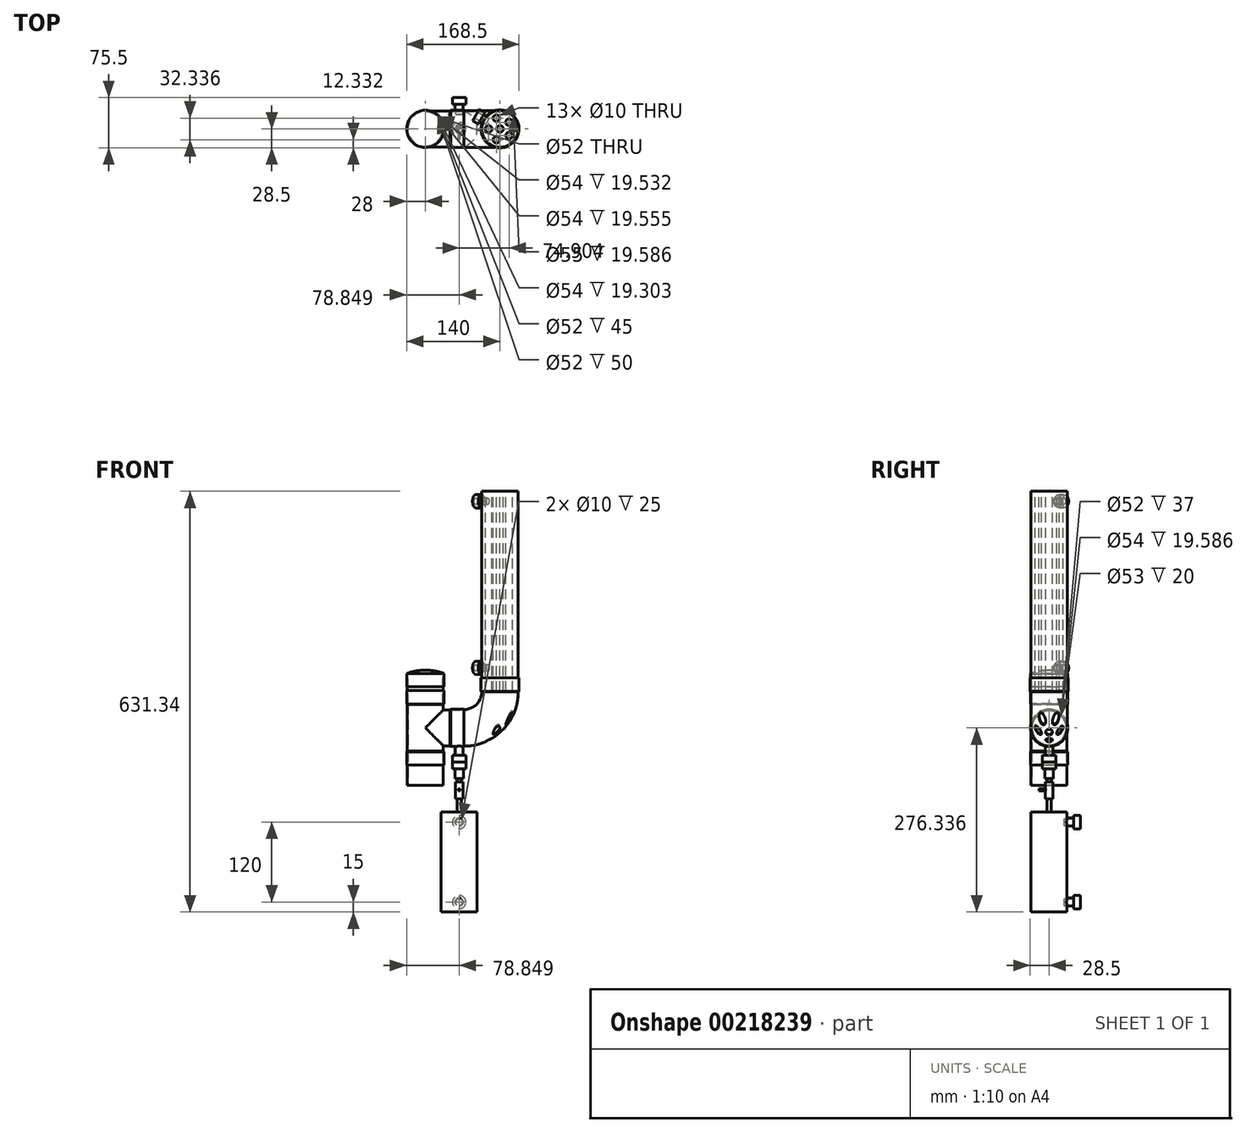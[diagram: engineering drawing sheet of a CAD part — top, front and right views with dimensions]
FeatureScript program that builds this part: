
annotation { "Feature Type Name" : "Feature", "Feature Type Description" : "" }
export const myFeature = defineFeature(function(context is Context, id is Id, definition is map)
    precondition{}
    {
        {
            var Q0;
            Q0=qCreatedBy(makeId("Top.planeOp"),FACE);
            var sketch = newSketch(context, id + "F0", { "sketchPlane" : qUnion([Q0])});
            skCircle(sketch, "E0", {"center": v(0, 0) * mm, "radius": 27 * mm});
            skCircle(sketch, "E1.0", {"center": v(0, 0) * mm, "radius": 26 * mm});
            skSolve(sketch);
        }
        {
            var Q0;
            Q0 = qSketchRegion(id + "F0", true);
            extrude(context, id + "F1", {"entities" : qUnion([Q0]), "depth" : 50 * mm, "symmetric" : true});
        }
        {
            var Q0;
            Q0=qCreatedBy(makeId("Front.planeOp"),FACE);
            var sketch = newSketch(context, id + "F2", { "sketchPlane" : qUnion([Q0])});
            skLineSegment(sketch, "E2", {"start": v(-27, 96.3) * mm, "end": v(-27, 26.3) * mm});
            skLineSegment(sketch, "E3", {"start": v(-27, 26.3) * mm, "end": v(-28, 25.47) * mm});
            skLineSegment(sketch, "E4", {"start": v(-28, 25.47) * mm, "end": v(-28, 5.47) * mm});
            skLineSegment(sketch, "E5", {"start": v(-28, 5.47) * mm, "end": v(-27, 5.47) * mm});
            skLineSegment(sketch, "E6", {"start": v(-27, 5.47) * mm, "end": v(-27, 25) * mm});
            skLineSegment(sketch, "E7", {"start": v(-27, 25) * mm, "end": v(-26, 25.83) * mm});
            skLineSegment(sketch, "E8", {"start": v(-26, 25.83) * mm, "end": v(-26, 96.75) * mm});
            skLineSegment(sketch, "E9.0", {"start": v(-27, 25) * mm, "end": v(27, 25) * mm, "construction": true});
            skLineSegment(sketch, "E10", {"start": v(-28, 25.47) * mm, "end": v(-28, 106.44) * mm, "construction": true});
            skLineSegment(sketch, "E11", {"start": v(-27, 96.3) * mm, "end": v(-28, 97.2) * mm});
            skLineSegment(sketch, "E12", {"start": v(-28, 97.2) * mm, "end": v(-28, 117.2) * mm});
            skLineSegment(sketch, "E13", {"start": v(-28, 117.2) * mm, "end": v(-27, 117.2) * mm});
            skLineSegment(sketch, "E14", {"start": v(-27, 117.2) * mm, "end": v(-27, 97.65) * mm});
            skLineSegment(sketch, "E15", {"start": v(-27, 97.65) * mm, "end": v(-26, 96.75) * mm});
            skSolve(sketch);
        }
        {
            var Q0;
            Q0 = qSketchRegion(id + "F2", true);
            var Q1;
            Q1=makeQuery(id+"F1.opExtrude","CAP_EDGE",EDGE,{"disambiguationData":[OSD([sQuery(id+"F0.wireOp",EDGE,"E0")])],"isStart":false});
            revolve(context, id + "F3", {"entities" : qUnion([Q0]), "axis" : qUnion([Q1]), "revolveType" : RevolveType.FULL});
        }
        {
            var Q0;
            Q0=qCreatedBy(makeId("Right.planeOp"),FACE);
            cPlane(context, id + "F4", {"entities" : qUnion([Q0]), "cplaneType" : CPlaneType.OFFSET, "offset" : (54 / 2 + 10) * mm, "width" : 150 * mm, "height" : 150 * mm});
        }
        {
            var Q0;
            Q0=qCreatedBy(id+"F4.planeOp",FACE);
            var sketch = newSketch(context, id + "F5", { "sketchPlane" : qUnion([Q0])});
            skCircle(sketch, "E16", {"center": v(0, 61.34) * mm, "radius": 27 * mm});
            skLineSegment(sketch, "E17.0", {"start": v(28, 117.2) * mm, "end": v(-28, 117.2) * mm, "construction": true});
            skLineSegment(sketch, "E18.0", {"start": v(28, 5.47) * mm, "end": v(-28, 5.47) * mm, "construction": true});
            skLineSegment(sketch, "E19", {"start": v(-40.75, 61.34) * mm, "end": v(41.53, 61.34) * mm, "construction": true});
            skSolve(sketch);
        }
        {
            var Q0;
            Q0 = qSketchRegion(id + "F5", true);
            var Q1;
            Q1=makeQuery(id+"F3.opRevolve","SWEPT_FACE",FACE,{"disambiguationData":[OSD([sQuery(id+"F2.wireOp",EDGE,"E2")])]});
            extrude(context, id + "F6", {"entities" : qUnion([Q0]), "operationType" : NewBodyOperationType.ADD, "endBound" : BoundingType.UP_TO_SURFACE, "oppositeDirection" : true, "endBoundEntityFace" : qUnion([Q1]), "depth" : 25 * mm});
        }
        {
            var Q0;
            Q0=makeQuery(id+"F6.opExtrude","CAP_FACE",FACE,{"disambiguationData":[OSD([sQuery(id+"F5.wireOp",EDGE,"E16")])],"isStart":true});
            var sketch = newSketch(context, id + "F7", { "sketchPlane" : qUnion([Q0])});
            skCircle(sketch, "E20", {"center": v(0, 61.34) * mm, "radius": 26 * mm});
            skSolve(sketch);
        }
        {
            var Q0;
            Q0 = qSketchRegion(id + "F7", true);
            var Q1;
            Q1=makeQuery(id+"F3.opRevolve","SWEPT_FACE",FACE,{"disambiguationData":[OSD([sQuery(id+"F2.wireOp",EDGE,"E8")])]});
            extrude(context, id + "F8", {"entities" : qUnion([Q0]), "operationType" : NewBodyOperationType.REMOVE, "endBound" : BoundingType.UP_TO_SURFACE, "oppositeDirection" : true, "endBoundEntityFace" : qUnion([Q1]), "depth" : 25 * mm});
        }
        {
            var Q0;
            Q0=makeQuery(id+"F3.opRevolve","SWEPT_FACE",FACE,{"disambiguationData":[OSD([sQuery(id+"F2.wireOp",EDGE,"E13")])]});
            var sketch = newSketch(context, id + "F9", { "sketchPlane" : qUnion([Q0])});
            skCircle(sketch, "E21.0", {"center": v(0, 0) * mm, "radius": 27 * mm});
            skCircle(sketch, "E22.0", {"center": v(0, 0) * mm, "radius": 26 * mm});
            skSolve(sketch);
        }
        {
            var Q0;
            Q0 = qSketchRegion(id + "F9", true);
            extrude(context, id + "F10", {"entities" : qUnion([Q0]), "oppositeDirection" : true, "depth" : 20 * mm, "hasSecondDirection" : true, "secondDirectionOppositeDirection" : false, "secondDirectionDepth" : 25 * mm});
        }
        {
            var Q0;
            Q0=qCreatedBy(makeId("Front.planeOp"),FACE);
            var sketch = newSketch(context, id + "F11", { "sketchPlane" : qUnion([Q0])});
            skLineSegment(sketch, "E23", {"start": v(-27, 142.2) * mm, "end": v(-27, 122.9) * mm});
            skLineSegment(sketch, "E24", {"start": v(-27, 122.9) * mm, "end": v(-28, 122.9) * mm});
            skLineSegment(sketch, "E25", {"start": v(-28, 122.9) * mm, "end": v(-28, 142.9) * mm});
            skLineSegment(sketch, "E26.0", {"start": v(27, 142.2) * mm, "end": v(-27, 142.2) * mm, "construction": true});
            skLineSegment(sketch, "E27", {"start": v(0, 142.2) * mm, "end": v(0, 164.67) * mm, "construction": true});
            skPoint(sketch, "E27.endSnap0", {"position": v(0, 142.2) * mm});
            skArc(sketch, "E28", {"start": v(0, 147.96) * mm, "mid": v(-14.23, 146.69) * mm, "end": v(-28, 142.9) * mm});
            skLineSegment(sketch, "E29", {"start": v(0, 142.2) * mm, "end": v(0, 31.65) * mm, "construction": true});
            skArc(sketch, "E30", {"start": v(-27, 142.2) * mm, "mid": v(-13.7, 145.76) * mm, "end": v(0, 146.96) * mm});
            skLineSegment(sketch, "E31", {"start": v(0, 146.96) * mm, "end": v(0, 147.96) * mm});
            skSolve(sketch);
        }
        {
            var Q0;
            Q0 = qSketchRegion(id + "F11", true);
            var Q1;
            Q1=makeQuery(id+"F10.opExtrude","CAP_EDGE",EDGE,{"disambiguationData":[OSD([sQuery(id+"F9.wireOp",EDGE,"E21.0")])],"isStart":true});
            revolve(context, id + "F12", {"entities" : qUnion([Q0]), "axis" : qUnion([Q1]), "revolveType" : RevolveType.FULL});
        }
        {
            var Q0;
            Q0=qCreatedBy(makeId("Front.planeOp"),FACE);
            var sketch = newSketch(context, id + "F13", { "sketchPlane" : qUnion([Q0])});
            skLineSegment(sketch, "E32", {"start": v(58, 89.34) * mm, "end": v(38, 89.34) * mm});
            skLineSegment(sketch, "E33", {"start": v(38, 89.34) * mm, "end": v(37, 88.34) * mm});
            skLineSegment(sketch, "E34", {"start": v(37, 88.34) * mm, "end": v(37, 86.92) * mm});
            skLineSegment(sketch, "E35", {"start": v(37, 86.92) * mm, "end": v(38.41, 88.34) * mm});
            skLineSegment(sketch, "E36", {"start": v(38.41, 88.34) * mm, "end": v(58, 88.34) * mm});
            skLineSegment(sketch, "E37", {"start": v(58, 88.34) * mm, "end": v(58, 89.34) * mm});
            skLineSegment(sketch, "E38", {"start": v(38.41, 88.34) * mm, "end": v(29.2, 88.34) * mm, "construction": true});
            skLineSegment(sketch, "E39.0", {"start": v(37, 88.34) * mm, "end": v(37, 34.34) * mm, "construction": true});
            skSolve(sketch);
        }
        {
            var Q0;
            Q0 = qSketchRegion(id + "F13", true);
            var Q1;
            Q1=makeQuery(id+"F6.opExtrude","CAP_EDGE",EDGE,{"disambiguationData":[OSD([sQuery(id+"F5.wireOp",EDGE,"E16")])],"isStart":true});
            revolve(context, id + "F14", {"operationType" : NewBodyOperationType.ADD, "entities" : qUnion([Q0]), "axis" : qUnion([Q1]), "revolveType" : RevolveType.FULL});
        }
        {
            var Q0;
            Q0=qCreatedBy(makeId("Front.planeOp"),FACE);
            var sketch = newSketch(context, id + "F15", { "sketchPlane" : qUnion([Q0])});
            skLineSegment(sketch, "E40", {"start": v(58, 61.34) * mm, "end": v(157.97, 61.34) * mm, "construction": true});
            skLineSegment(sketch, "E41", {"start": v(58, 89.34) * mm, "end": v(106.65, 89.34) * mm, "construction": true});
            skLineSegment(sketch, "E42", {"start": v(58, 33.34) * mm, "end": v(107.57, 33.34) * mm, "construction": true});
            skArc(sketch, "E43", {"start": v(58, 61.34) * mm, "mid": v(96.18, 77.15) * mm, "end": v(112, 115.34) * mm});
            skLineSegment(sketch, "E44", {"start": v(58, 89.34) * mm, "end": v(58, 145) * mm, "construction": true});
            skLineSegment(sketch, "E45", {"start": v(58, 115.34) * mm, "end": v(151.68, 115.34) * mm, "construction": true});
            skLineSegment(sketch, "E46.0", {"start": v(58, 33.34) * mm, "end": v(58, 89.34) * mm, "construction": true});
            skLineSegment(sketch, "E47", {"start": v(58, 61.34) * mm, "end": v(38, 61.34) * mm});
            skSolve(sketch);
        }
        {
            var Q0;
            Q0=makeQuery(id+"F14.opRevolve","SWEPT_FACE",FACE,{"disambiguationData":[OSD([sQuery(id+"F13.wireOp",EDGE,"E37")])]});
            cPlane(context, id + "F16", {"entities" : qUnion([Q0]), "cplaneType" : CPlaneType.OFFSET, "offset" : 20 * mm, "oppositeDirection" : true, "width" : 150 * mm, "height" : 150 * mm});
        }
        {
            var Q0;
            Q0=qCreatedBy(id+"F16.planeOp",FACE);
            var sketch = newSketch(context, id + "F17", { "sketchPlane" : qUnion([Q0])});
            skCircle(sketch, "E48.0", {"center": v(0, 61.34) * mm, "radius": 26.5 * mm});
            skCircle(sketch, "E49.0", {"center": v(0, 61.34) * mm, "radius": 27.5 * mm});
            skSolve(sketch);
        }
        {
            var Q0;
            Q0 = qSketchRegion(id + "F17", true);
            var Q1;
            Q1 = qConstructionFilter(qBodyType(qCreatedBy(id + "F15" ,EDGE), BodyType.WIRE), ConstructionObject.NO);
            sweep(context, id + "F18", {"profiles" : qUnion([Q0]), "path" : qUnion([Q1])});
        }
        {
            var Q0;
            Q0=qCreatedBy(makeId("Front.planeOp"),FACE);
            var sketch = newSketch(context, id + "F19", { "sketchPlane" : qUnion([Q0])});
            skLineSegment(sketch, "E50", {"start": v(83.5, 136.34) * mm, "end": v(83.5, 116.34) * mm});
            skLineSegment(sketch, "E51", {"start": v(83.5, 116.34) * mm, "end": v(84.5, 115.34) * mm});
            skLineSegment(sketch, "E52", {"start": v(84.5, 115.34) * mm, "end": v(85.91, 115.34) * mm});
            skLineSegment(sketch, "E53", {"start": v(85.91, 115.34) * mm, "end": v(84.5, 116.75) * mm});
            skLineSegment(sketch, "E54", {"start": v(84.5, 116.75) * mm, "end": v(84.5, 136.34) * mm});
            skLineSegment(sketch, "E55", {"start": v(84.5, 136.34) * mm, "end": v(83.5, 136.34) * mm});
            skLineSegment(sketch, "E56", {"start": v(84.5, 115.34) * mm, "end": v(84.5, 127.62) * mm, "construction": true});
            skLineSegment(sketch, "E57.0", {"start": v(84.5, 115.34) * mm, "end": v(139.5, 115.34) * mm, "construction": true});
            skSolve(sketch);
        }
        {
            var Q0;
            Q0 = qSketchRegion(id + "F19", true);
            var Q1;
            Q1=makeQuery(id+"F18.opSweep","CAP_EDGE",EDGE,{"disambiguationData":[OSD([sQuery(id+"F15.wireOp",VERTEX,"E43.end"),sQuery(id+"F17.wireOp",EDGE,"E49.0")])],"isStart":false});
            revolve(context, id + "F20", {"operationType" : NewBodyOperationType.ADD, "entities" : qUnion([Q0]), "axis" : qUnion([Q1]), "revolveType" : RevolveType.FULL});
        }
        {
            var Q0;
            Q0=makeQuery(id+"F20.opRevolve","SWEPT_FACE",FACE,{"disambiguationData":[OSD([sQuery(id+"F19.wireOp",EDGE,"E55")])]});
            cPlane(context, id + "F21", {"entities" : qUnion([Q0]), "cplaneType" : CPlaneType.OFFSET, "offset" : 20 * mm, "oppositeDirection" : true, "width" : 150 * mm, "height" : 150 * mm});
        }
        {
            var Q0;
            Q0=qCreatedBy(id+"F21.planeOp",FACE);
            var sketch = newSketch(context, id + "F22", { "sketchPlane" : qUnion([Q0])});
            skCircle(sketch, "E58.0", {"center": v(112, 0) * mm, "radius": 27.5 * mm});
            skSolve(sketch);
        }
        {
            var Q0;
            Q0 = qSketchRegion(id + "F22", true);
            extrude(context, id + "F23", {"entities" : qUnion([Q0]), "depth" : 300 * mm});
        }
        {
            var Q0;
            Q0=makeQuery(id+"F23.opExtrude","CAP_FACE",FACE,{"disambiguationData":[OSD([sQuery(id+"F22.wireOp",EDGE,"E58.0")])],"isStart":false});
            var sketch = newSketch(context, id + "F24", { "sketchPlane" : qUnion([Q0])});
            skCircle(sketch, "E59", {"center": v(112, 0) * mm, "radius": 6 * mm});
            skCircle(sketch, "E60", {"center": v(95, 0) * mm, "radius": 6 * mm});
            skCircle(sketch, "E61.1.0", {"center": v(106.75, -16.17) * mm, "radius": 6 * mm});
            skCircle(sketch, "E61.2.0", {"center": v(125.75, -10) * mm, "radius": 6 * mm});
            skCircle(sketch, "E61.3.0", {"center": v(125.75, 10) * mm, "radius": 6 * mm});
            skCircle(sketch, "E61.4.0", {"center": v(106.75, 16.17) * mm, "radius": 6 * mm});
            skSolve(sketch);
        }
        {
            var Q0;
            Q0 = qSketchRegion(id + "F24", true);
            extrude(context, id + "F25", {"entities" : qUnion([Q0]), "oppositeDirection" : true, "depth" : 300 * mm});
        }
        {
            var Q0;
            Q0=makeQuery(id+"F23.opExtrude","CAP_FACE",FACE,{"disambiguationData":[OSD([sQuery(id+"F22.wireOp",EDGE,"E58.0")])],"isStart":false});
            var sketch = newSketch(context, id + "F26", { "sketchPlane" : qUnion([Q0])});
            skCircle(sketch, "E62", {"center": v(112, 0) * mm, "radius": 5 * mm});
            skCircle(sketch, "E63", {"center": v(106.75, -16.17) * mm, "radius": 5 * mm});
            skCircle(sketch, "E64", {"center": v(125.75, -10) * mm, "radius": 5 * mm});
            skCircle(sketch, "E65", {"center": v(125.75, 10) * mm, "radius": 5 * mm});
            skCircle(sketch, "E66", {"center": v(106.75, 16.17) * mm, "radius": 5 * mm});
            skCircle(sketch, "E67", {"center": v(95, 0) * mm, "radius": 5 * mm});
            skSolve(sketch);
        }
        {
            var Q0;
            Q0 = qSketchRegion(id + "F26", true);
            extrude(context, id + "F27", {"entities" : qUnion([Q0]), "operationType" : NewBodyOperationType.REMOVE, "endBound" : BoundingType.THROUGH_ALL, "oppositeDirection" : true, "depth" : 25 * mm});
        }
        {
            var Q0;
            Q0=makeQuery(id+"F25.opExtrude","SWEPT_BODY",BODY,{"disambiguationData":[OSD([sQuery(id+"F24.wireOp",EDGE,"E61.1.0")])]});
            var Q1;
            Q1=makeQuery(id+"F23.opExtrude","SWEPT_BODY",BODY,{"disambiguationData":[OSD([sQuery(id+"F22.wireOp",EDGE,"E58.0")])]});
            var Q2;
            Q2=makeQuery(id+"F25.opExtrude","SWEPT_BODY",BODY,{"disambiguationData":[OSD([sQuery(id+"F24.wireOp",EDGE,"E61.3.0")])]});
            var Q3;
            Q3=makeQuery(id+"F25.opExtrude","SWEPT_BODY",BODY,{"disambiguationData":[OSD([sQuery(id+"F24.wireOp",EDGE,"E59")])]});
            var Q4;
            Q4=makeQuery(id+"F25.opExtrude","SWEPT_BODY",BODY,{"disambiguationData":[OSD([sQuery(id+"F24.wireOp",EDGE,"E60")])]});
            var Q5;
            Q5=makeQuery(id+"F25.opExtrude","SWEPT_BODY",BODY,{"disambiguationData":[OSD([sQuery(id+"F24.wireOp",EDGE,"E61.2.0")])]});
            var Q6;
            Q6=makeQuery(id+"F25.opExtrude","SWEPT_BODY",BODY,{"disambiguationData":[OSD([sQuery(id+"F24.wireOp",EDGE,"E61.4.0")])]});
            booleanBodies(context, id + "F28", {"operationType" : BooleanOperationType.UNION, "tools" : qUnion([Q0, Q1, Q2, Q3, Q4, Q5, Q6])});
        }
        {
            var Q0;
            Q0=qCreatedBy(makeId("Top.planeOp"),FACE);
            cPlane(context, id + "F29", {"entities" : qUnion([Q0]), "cplaneType" : CPlaneType.OFFSET, "offset" : 20 * mm, "width" : 150 * mm, "height" : 150 * mm});
        }
        {
            var Q0;
            Q0=qCreatedBy(id+"F29.planeOp",FACE);
            var sketch = newSketch(context, id + "F30", { "sketchPlane" : qUnion([Q0])});
            skCircle(sketch, "E68", {"center": v(50.85, 0) * mm, "radius": 6 * mm});
            skSolve(sketch);
        }
        {
            var Q0;
            Q0 = qSketchRegion(id + "F30", true);
            var Q1;
            Q1=makeQuery(id+"F14.opRevolve","SWEPT_FACE",FACE,{"disambiguationData":[OSD([sQuery(id+"F13.wireOp",EDGE,"E32")])]});
            extrude(context, id + "F31", {"entities" : qUnion([Q0]), "operationType" : NewBodyOperationType.ADD, "endBound" : BoundingType.UP_TO_SURFACE, "endBoundEntityFace" : qUnion([Q1]), "depth" : 25 * mm});
        }
        {
            var Q0;
            Q0=makeQuery(id+"F31.opExtrude","CAP_FACE",FACE,{"disambiguationData":[OSD([sQuery(id+"F30.wireOp",EDGE,"E68")])],"isStart":true});
            var sketch = newSketch(context, id + "F32", { "sketchPlane" : qUnion([Q0])});
            skCircle(sketch, "E69", {"center": v(50.85, 0) * mm, "radius": 5 * mm});
            skSolve(sketch);
        }
        {
            var Q0;
            Q0 = qSketchRegion(id + "F32", true);
            extrude(context, id + "F33", {"entities" : qUnion([Q0]), "operationType" : NewBodyOperationType.REMOVE, "oppositeDirection" : true, "depth" : 50 * mm});
        }
        {
            var Q0;
            Q0=qCreatedBy(id+"F29.planeOp",FACE);
            var sketch = newSketch(context, id + "F34", { "sketchPlane" : qUnion([Q0])});
            skCircle(sketch, "E70", {"center": v(50.85, 0) * mm, "radius": 10 * mm});
            skSolve(sketch);
        }
        {
            var Q0;
            Q0 = qSketchRegion(id + "F34", true);
            extrude(context, id + "F35", {"entities" : qUnion([Q0]), "operationType" : NewBodyOperationType.ADD, "oppositeDirection" : true, "depth" : 10 * mm});
        }
        {
            var Q0;
            Q0=makeQuery(id+"F35.opExtrude","CAP_FACE",FACE,{"disambiguationData":[OSD([sQuery(id+"F34.wireOp",EDGE,"E70")])],"isStart":false});
            var sketch = newSketch(context, id + "F36", { "sketchPlane" : qUnion([Q0])});
            skCircle(sketch, "E71.0", {"center": v(50.85, 0) * mm, "radius": 10 * mm});
            skSolve(sketch);
        }
        {
            var Q0;
            Q0 = qSketchRegion(id + "F36", true);
            extrude(context, id + "F37", {"entities" : qUnion([Q0]), "depth" : 10 * mm});
        }
        {
            var Q0;
            Q0=makeQuery(id+"F37.opExtrude","CAP_FACE",FACE,{"disambiguationData":[OSD([sQuery(id+"F36.wireOp",EDGE,"E71.0")])],"isStart":false});
            var sketch = newSketch(context, id + "F38", { "sketchPlane" : qUnion([Q0])});
            skCircle(sketch, "E72", {"center": v(50.85, 0) * mm, "radius": 6.43 * mm});
            skSolve(sketch);
        }
        {
            var Q0;
            Q0 = qSketchRegion(id + "F38", true);
            extrude(context, id + "F39", {"entities" : qUnion([Q0]), "operationType" : NewBodyOperationType.ADD, "depth" : 15 * mm});
        }
        {
            var Q0;
            Q0=makeQuery(id+"F39.opExtrude","CAP_FACE",FACE,{"disambiguationData":[OSD([sQuery(id+"F38.wireOp",EDGE,"E72")])],"isStart":false});
            var sketch = newSketch(context, id + "F40", { "sketchPlane" : qUnion([Q0])});
            skCircle(sketch, "E73", {"center": v(50.85, 0) * mm, "radius": 3 * mm});
            skSolve(sketch);
        }
        {
            var Q0;
            Q0 = qSketchRegion(id + "F40", true);
            extrude(context, id + "F41", {"entities" : qUnion([Q0]), "operationType" : NewBodyOperationType.ADD, "depth" : 5 * mm});
        }
        {
            var Q0;
            Q0=makeQuery(id+"F41.opExtrude","CAP_FACE",FACE,{"disambiguationData":[OSD([sQuery(id+"F40.wireOp",EDGE,"E73")])],"isStart":false});
            var sketch = newSketch(context, id + "F42", { "sketchPlane" : qUnion([Q0])});
            skCircle(sketch, "E74", {"center": v(50.85, 0) * mm, "radius": 5.5 * mm});
            skSolve(sketch);
        }
        {
            var Q0;
            Q0 = qSketchRegion(id + "F42", true);
            extrude(context, id + "F43", {"entities" : qUnion([Q0]), "operationType" : NewBodyOperationType.ADD, "depth" : 25 * mm});
        }
        {
            var Q0;
            Q0=qCreatedBy(makeId("Front.planeOp"),FACE);
            var sketch = newSketch(context, id + "F44", { "sketchPlane" : qUnion([Q0])});
            skCircle(sketch, "E75", {"center": v(50.94, -31.61) * mm, "radius": 1.5 * mm});
            skSolve(sketch);
        }
        {
            var Q0;
            Q0 = qSketchRegion(id + "F44", true);
            extrude(context, id + "F45", {"entities" : qUnion([Q0]), "operationType" : NewBodyOperationType.ADD, "depth" : 15 * mm});
        }
        {
            var Q0;
            Q0=makeQuery(id+"F43.opExtrude","CAP_FACE",FACE,{"disambiguationData":[OSD([sQuery(id+"F42.wireOp",EDGE,"E74")])],"isStart":false});
            var sketch = newSketch(context, id + "F46", { "sketchPlane" : qUnion([Q0])});
            skCircle(sketch, "E76", {"center": v(50.85, 0) * mm, "radius": 3 * mm});
            skSolve(sketch);
        }
        {
            var Q0;
            Q0 = qSketchRegion(id + "F46", true);
            extrude(context, id + "F47", {"entities" : qUnion([Q0]), "operationType" : NewBodyOperationType.ADD, "depth" : 20 * mm});
        }
        {
            var Q0;
            Q0=makeQuery(id+"F47.opExtrude","CAP_FACE",FACE,{"disambiguationData":[OSD([sQuery(id+"F46.wireOp",EDGE,"E76")])],"isStart":false});
            var sketch = newSketch(context, id + "F48", { "sketchPlane" : qUnion([Q0])});
            skCircle(sketch, "E77", {"center": v(50.85, 0) * mm, "radius": 27 * mm});
            skSolve(sketch);
        }
        {
            var Q0;
            Q0 = qSketchRegion(id + "F48", true);
            extrude(context, id + "F49", {"entities" : qUnion([Q0]), "operationType" : NewBodyOperationType.ADD, "depth" : 150 * mm});
        }
        {
            var Q0;
            Q0=qCreatedBy(id+"F4.planeOp",FACE);
            var sketch = newSketch(context, id + "F50", { "sketchPlane" : qUnion([Q0])});
            skLineSegment(sketch, "E78", {"start": v(69.58, 75.8) * mm, "end": v(69.58, -40.07) * mm, "construction": true});
            skLineSegment(sketch, "E79", {"start": v(-66.33, 75.8) * mm, "end": v(-66.33, -31.95) * mm, "construction": true});
            skSolve(sketch);
        }
        {
            var Q0;
            Q0=sQuery(id+"F50.wireOp",EDGE,"E79");
            var Q1;
            Q1=sQuery(id+"F50.wireOp",EDGE,"E78");
            cPlane(context, id + "F51", {"entities" : qUnion([Q0, Q1]), "cplaneType" : CPlaneType.LINE_ANGLE, "offset" : 25 * mm, "angle" : 30 * degree, "width" : 150 * mm, "height" : 150 * mm});
        }
        {
            var Q0;
            Q0=qCreatedBy(id+"F51.planeOp",FACE);
            var sketch = newSketch(context, id + "F52", { "sketchPlane" : qUnion([Q0])});
            skCircle(sketch, "E80", {"center": v(56, 151.34) * mm, "radius": 6 * mm});
            skCircle(sketch, "E81", {"center": v(56, 401.34) * mm, "radius": 6 * mm});
            skLineSegment(sketch, "E82.0", {"start": v(28.5, 416.34) * mm, "end": v(83.5, 416.34) * mm, "construction": true});
            skLineSegment(sketch, "E83.0", {"start": v(84.5, 136.34) * mm, "end": v(27.5, 136.34) * mm, "construction": true});
            skLineSegment(sketch, "E84", {"start": v(83.5, 416.34) * mm, "end": v(84.5, 136.34) * mm, "construction": true});
            skLineSegment(sketch, "E85", {"start": v(28.5, 416.34) * mm, "end": v(27.5, 136.34) * mm, "construction": true});
            skLineSegment(sketch, "E86", {"start": v(56, 442.1) * mm, "end": v(56, 121.02) * mm, "construction": true});
            skPoint(sketch, "E86.startSnap0", {"position": v(56, 416.34) * mm});
            skPoint(sketch, "E86.endSnap0", {"position": v(56, 136.34) * mm});
            skSolve(sketch);
        }
        {
            var Q0;
            Q0 = qSketchRegion(id + "F52", true);
            var Q1;
            Q1=makeQuery(id+"F23.opExtrude","SWEPT_FACE",FACE,{"disambiguationData":[OSD([sQuery(id+"F22.wireOp",EDGE,"E58.0")])]});
            extrude(context, id + "F53", {"entities" : qUnion([Q0]), "operationType" : NewBodyOperationType.ADD, "endBound" : BoundingType.UP_TO_SURFACE, "endBoundEntityFace" : qUnion([Q1]), "depth" : 25 * mm});
        }
        {
            var Q0;
            Q0=makeQuery(id+"F53.opExtrude","CAP_FACE",FACE,{"disambiguationData":[OSD([sQuery(id+"F52.wireOp",EDGE,"E81")])],"isStart":true});
            var sketch = newSketch(context, id + "F54", { "sketchPlane" : qUnion([Q0])});
            skCircle(sketch, "E87", {"center": v(-56, 401.34) * mm, "radius": 5 * mm});
            skCircle(sketch, "E88", {"center": v(-56, 151.34) * mm, "radius": 5 * mm});
            skSolve(sketch);
        }
        {
            var Q0;
            Q0 = qSketchRegion(id + "F54", true);
            extrude(context, id + "F55", {"entities" : qUnion([Q0]), "operationType" : NewBodyOperationType.REMOVE, "oppositeDirection" : true, "depth" : 10 * mm});
        }
        {
            var Q0;
            Q0=makeQuery(id+"F53.opExtrude","CAP_FACE",FACE,{"disambiguationData":[OSD([sQuery(id+"F52.wireOp",EDGE,"E81")])],"isStart":true});
            var sketch = newSketch(context, id + "F56", { "sketchPlane" : qUnion([Q0])});
            skCircle(sketch, "E89", {"center": v(-56, 401.34) * mm, "radius": 10 * mm});
            skCircle(sketch, "E90.0", {"center": v(-56, 401.34) * mm, "radius": 5 * mm});
            skCircle(sketch, "E91.0", {"center": v(-56, 151.34) * mm, "radius": 5 * mm});
            skCircle(sketch, "E92", {"center": v(-56, 151.34) * mm, "radius": 10 * mm});
            skSolve(sketch);
        }
        {
            var Q0;
            Q0 = qSketchRegion(id + "F56", true);
            extrude(context, id + "F57", {"entities" : qUnion([Q0]), "operationType" : NewBodyOperationType.ADD, "depth" : 10 * mm});
        }
        {
            var Q0;
            Q0=qCreatedBy(makeId("Front.planeOp"),FACE);
            cPlane(context, id + "F58", {"entities" : qUnion([Q0]), "cplaneType" : CPlaneType.OFFSET, "offset" : (54 / 2 + 10) * mm, "oppositeDirection" : true, "width" : 150 * mm, "height" : 150 * mm});
        }
        {
            var Q0;
            Q0=qCreatedBy(id+"F58.planeOp",FACE);
            var sketch = newSketch(context, id + "F59", { "sketchPlane" : qUnion([Q0])});
            skLineSegment(sketch, "E93.0", {"start": v(77.85, -65) * mm, "end": v(23.85, -65) * mm, "construction": true});
            skLineSegment(sketch, "E94.0", {"start": v(77.85, -215) * mm, "end": v(23.85, -215) * mm, "construction": true});
            skCircle(sketch, "E95", {"center": v(50.85, -80) * mm, "radius": 6 * mm});
            skPoint(sketch, "E95.centerSnap0", {"position": v(50.85, -65) * mm});
            skCircle(sketch, "E96", {"center": v(50.85, -200) * mm, "radius": 6 * mm});
            skPoint(sketch, "E96.centerSnap0", {"position": v(50.85, -215) * mm});
            skSolve(sketch);
        }
        {
            var Q0;
            Q0 = qSketchRegion(id + "F59", true);
            var Q1;
            Q1=makeQuery(id+"F49.opExtrude","SWEPT_FACE",FACE,{"disambiguationData":[OSD([sQuery(id+"F48.wireOp",EDGE,"E77")])]});
            extrude(context, id + "F60", {"entities" : qUnion([Q0]), "operationType" : NewBodyOperationType.ADD, "endBound" : BoundingType.UP_TO_SURFACE, "endBoundEntityFace" : qUnion([Q1]), "depth" : 25 * mm});
        }
        {
            var Q0;
            Q0=makeQuery(id+"F60.opExtrude","CAP_FACE",FACE,{"disambiguationData":[OSD([sQuery(id+"F59.wireOp",EDGE,"E95")])],"isStart":true});
            var sketch = newSketch(context, id + "F61", { "sketchPlane" : qUnion([Q0])});
            skCircle(sketch, "E97", {"center": v(-50.85, -80) * mm, "radius": 10 * mm});
            skCircle(sketch, "E98", {"center": v(-50.85, -200) * mm, "radius": 10 * mm});
            skSolve(sketch);
        }
        {
            var Q0;
            Q0 = qSketchRegion(id + "F61", true);
            extrude(context, id + "F62", {"entities" : qUnion([Q0]), "operationType" : NewBodyOperationType.ADD, "depth" : 10 * mm});
        }
        {
            var Q0;
            Q0=makeQuery(id+"F62.opExtrude","CAP_FACE",FACE,{"disambiguationData":[OSD([sQuery(id+"F61.wireOp",EDGE,"E97")])],"isStart":false});
            var sketch = newSketch(context, id + "F63", { "sketchPlane" : qUnion([Q0])});
            skCircle(sketch, "E99", {"center": v(-50.85, -80) * mm, "radius": 5 * mm});
            skCircle(sketch, "E100", {"center": v(-50.85, -200) * mm, "radius": 5 * mm});
            skSolve(sketch);
        }
        {
            var Q0;
            Q0 = qSketchRegion(id + "F63", true);
            extrude(context, id + "F64", {"entities" : qUnion([Q0]), "operationType" : NewBodyOperationType.REMOVE, "oppositeDirection" : true, "depth" : 25 * mm});
        }
    });
